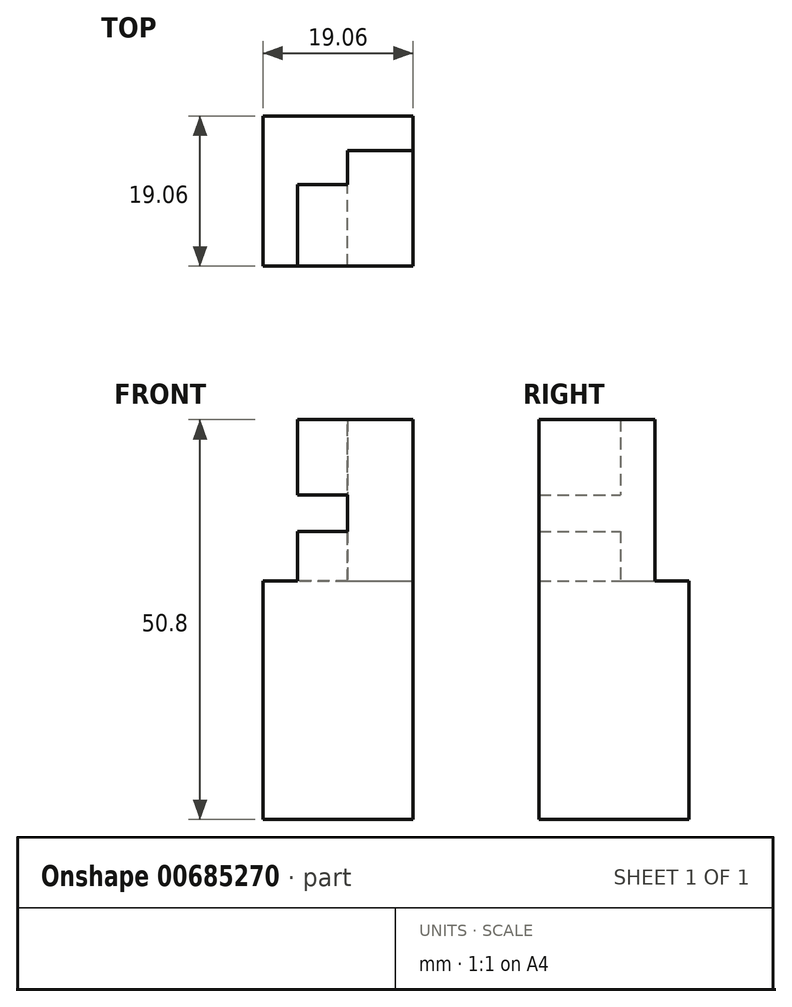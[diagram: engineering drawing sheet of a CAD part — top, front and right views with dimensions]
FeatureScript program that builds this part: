
annotation { "Feature Type Name" : "Feature", "Feature Type Description" : "" }
export const myFeature = defineFeature(function(context is Context, id is Id, definition is map)
    precondition{}
    {
        {
            var Q0;
            Q0=qCreatedBy(makeId("Top.planeOp"),FACE);
            var sketch = newSketch(context, id + "F0", { "sketchPlane" : qUnion([Q0])});
            skLineSegment(sketch, "E0.bottom", {"start": v(9.53, -9.52) * mm, "end": v(-9.53, -9.53) * mm});
            skLineSegment(sketch, "E0.top", {"start": v(9.53, 9.53) * mm, "end": v(-9.53, 9.52) * mm});
            skLineSegment(sketch, "E0.left", {"start": v(9.53, -9.52) * mm, "end": v(9.53, 9.53) * mm});
            skLineSegment(sketch, "E0.right", {"start": v(-9.53, -9.53) * mm, "end": v(-9.53, 9.52) * mm});
            skPoint(sketch, "E0.middle", {"position": v(0, 0) * mm});
            skSolve(sketch);
        }
        {
            var Q0;
            Q0=makeQuery(id+"F0.imprint","IMPRINT",FACE,{"disambiguationData":[TD([[makeQuery(id+"F0.imprint","IMPRINT",EDGE,{"derivedFrom":sQuery(id+"F0.wireOp",EDGE,"E0.bottom")}),-1.0]])]});
            extrude(context, id + "F1", {"entities" : qUnion([Q0]), "depth" : 50.8 * mm, "offsetDistance" : 25.4 * mm});
        }
        {
            var Q0;
            Q0=makeQuery(id+"F1.opExtrude","SWEPT_FACE",FACE,{"disambiguationData":[OSD([sQuery(id+"F0.wireOp",EDGE,"E0.left")])]});
            var sketch = newSketch(context, id + "F2", { "sketchPlane" : qUnion([Q0])});
            skLineSegment(sketch, "E1.bottom", {"start": v(9.53, 50.8) * mm, "end": v(5.16, 50.8) * mm});
            skLineSegment(sketch, "E1.top", {"start": v(9.53, 30.3) * mm, "end": v(5.16, 30.3) * mm});
            skLineSegment(sketch, "E1.left", {"start": v(9.53, 50.8) * mm, "end": v(9.53, 30.3) * mm});
            skLineSegment(sketch, "E1.right", {"start": v(5.16, 50.8) * mm, "end": v(5.16, 30.3) * mm});
            skSolve(sketch);
        }
        {
            var Q0;
            Q0=makeQuery(id+"F2.imprint","IMPRINT",FACE,{"disambiguationData":[TD([[makeQuery(id+"F2.imprint","IMPRINT",EDGE,{"derivedFrom":sQuery(id+"F2.wireOp",EDGE,"E1.bottom")}),-1.0]])]});
            extrude(context, id + "F3", {"entities" : qUnion([Q0]), "operationType" : NewBodyOperationType.REMOVE, "oppositeDirection" : true, "depth" : 25.4 * mm, "offsetDistance" : 25.4 * mm});
        }
        {
            var Q0;
            Q0=makeQuery(id+"F3.boolean.opBoolean","COPY",FACE,{"derivedFrom":makeQuery(id+"F3.opExtrude","SWEPT_FACE",FACE,{"disambiguationData":[OSD([sQuery(id+"F2.wireOp",EDGE,"E1.right")])]})});
            var sketch = newSketch(context, id + "F4", { "sketchPlane" : qUnion([Q0])});
            skLineSegment(sketch, "E2.bottom", {"start": v(9.53, 30.3) * mm, "end": v(5.13, 30.3) * mm});
            skLineSegment(sketch, "E2.top", {"start": v(9.52, 50.8) * mm, "end": v(5.13, 50.8) * mm});
            skLineSegment(sketch, "E2.left", {"start": v(9.53, 30.3) * mm, "end": v(9.52, 50.8) * mm});
            skLineSegment(sketch, "E2.right", {"start": v(5.13, 30.3) * mm, "end": v(5.13, 50.8) * mm});
            skSolve(sketch);
        }
        {
            var Q0;
            Q0=makeQuery(id+"F4.imprint","IMPRINT",FACE,{"disambiguationData":[TD([[makeQuery(id+"F4.imprint","IMPRINT",EDGE,{"derivedFrom":sQuery(id+"F4.wireOp",EDGE,"E2.bottom")}),-1.0]])]});
            extrude(context, id + "F5", {"entities" : qUnion([Q0]), "operationType" : NewBodyOperationType.REMOVE, "oppositeDirection" : true, "depth" : 25.4 * mm, "offsetDistance" : 25.4 * mm});
        }
        {
            var Q0;
            Q0=makeQuery(id+"F5.boolean.opBoolean","COPY",FACE,{"derivedFrom":makeQuery(id+"F5.opExtrude","SWEPT_FACE",FACE,{"disambiguationData":[OSD([sQuery(id+"F4.wireOp",EDGE,"E2.right")])]})});
            var sketch = newSketch(context, id + "F6", { "sketchPlane" : qUnion([Q0])});
            skLineSegment(sketch, "E3.bottom", {"start": v(-0.8, 50.8) * mm, "end": v(-5.16, 50.8) * mm});
            skLineSegment(sketch, "E3.top", {"start": v(-0.8, 26.3) * mm, "end": v(-5.16, 26.3) * mm});
            skLineSegment(sketch, "E3.left", {"start": v(-0.8, 50.8) * mm, "end": v(-0.8, 29.6) * mm});
            skLineSegment(sketch, "E3.right", {"start": v(-5.16, 50.8) * mm, "end": v(-5.16, 26.3) * mm});
            skLineSegment(sketch, "E4.bottom", {"start": v(-0.8, 26.3) * mm, "end": v(9.53, 26.3) * mm});
            skLineSegment(sketch, "E4.top", {"start": v(-0.8, 29.6) * mm, "end": v(9.53, 29.6) * mm});
            skLineSegment(sketch, "E4.right", {"start": v(9.53, 26.3) * mm, "end": v(9.53, 29.6) * mm});
            skSolve(sketch);
        }
        {
            var Q0;
            Q0=makeQuery(id+"F6.imprint","IMPRINT",FACE,{"disambiguationData":[TD([[makeQuery(id+"F6.imprint","IMPRINT",EDGE,{"derivedFrom":sQuery(id+"F6.wireOp",EDGE,"E3.bottom")}),1.0]])]});
            extrude(context, id + "F7", {"entities" : qUnion([Q0]), "operationType" : NewBodyOperationType.REMOVE, "oppositeDirection" : true, "depth" : 6.35 * mm, "offsetDistance" : 25.4 * mm});
        }
        {
            var Q0;
            Q0=makeQuery(id+"F7.boolean.opBoolean","COPY",FACE,{"derivedFrom":makeQuery(id+"F7.opExtrude","SWEPT_FACE",FACE,{"disambiguationData":[OSD([sQuery(id+"F6.wireOp",EDGE,"E3.left")])]})});
            var sketch = newSketch(context, id + "F8", { "sketchPlane" : qUnion([Q0])});
            skLineSegment(sketch, "E5.bottom", {"start": v(5.13, 41.23) * mm, "end": v(-1.22, 41.23) * mm});
            skLineSegment(sketch, "E5.top", {"start": v(5.13, 36.6) * mm, "end": v(-1.22, 36.6) * mm});
            skLineSegment(sketch, "E5.left", {"start": v(5.13, 41.23) * mm, "end": v(5.13, 36.6) * mm});
            skLineSegment(sketch, "E5.right", {"start": v(-1.22, 41.23) * mm, "end": v(-1.22, 36.6) * mm});
            skSolve(sketch);
        }
        {
            var Q0;
            Q0 = qSketchRegion(id + "F1gJe40UKmXpRf7_1", true);
            var Q1;
            Q1=makeQuery(id+"F8.imprint","IMPRINT",FACE,{"disambiguationData":[TD([[makeQuery(id+"F8.imprint","IMPRINT",EDGE,{"derivedFrom":sQuery(id+"F8.wireOp",EDGE,"E5.bottom")}),1.0]])]});
            extrude(context, id + "F9", {"entities" : qUnion([Q0, Q1]), "operationType" : NewBodyOperationType.REMOVE, "oppositeDirection" : true, "depth" : 25.4 * mm, "offsetDistance" : 25.4 * mm});
        }
    });
